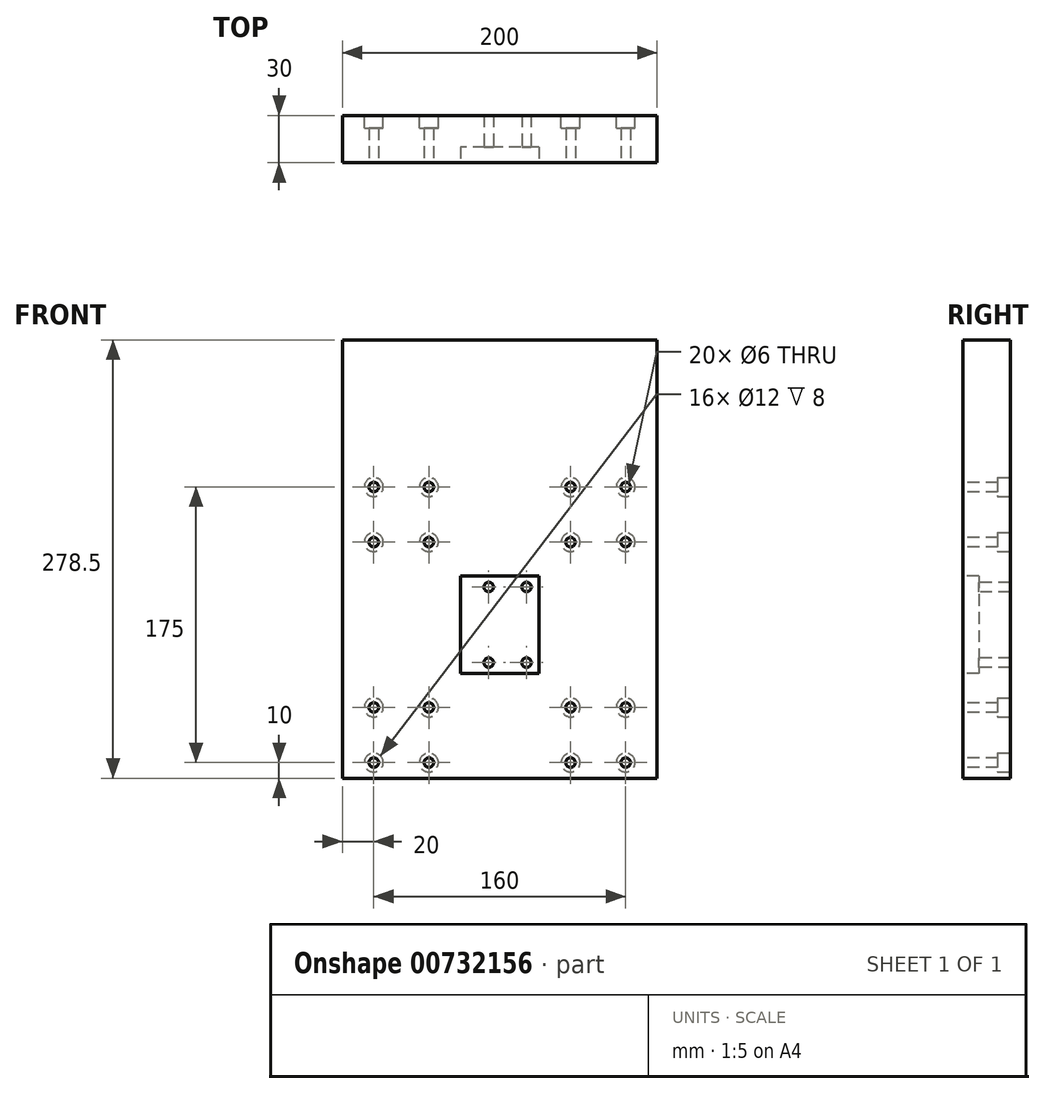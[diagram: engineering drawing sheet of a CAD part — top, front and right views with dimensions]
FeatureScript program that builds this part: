
annotation { "Feature Type Name" : "Feature", "Feature Type Description" : "" }
export const myFeature = defineFeature(function(context is Context, id is Id, definition is map)
    precondition{}
    {
        {
            var Q0;
            Q0=qCreatedBy(makeId("Front.planeOp"),FACE);
            var sketch = newSketch(context, id + "F0", { "sketchPlane" : qUnion([Q0])});
            skLineSegment(sketch, "E0.bottom", {"start": v(0, 0) * mm, "end": v(200, 0) * mm});
            skLineSegment(sketch, "E0.top", {"start": v(0, 400) * mm, "end": v(200, 400) * mm});
            skLineSegment(sketch, "E0.left", {"start": v(0, 0) * mm, "end": v(0, 400) * mm});
            skLineSegment(sketch, "E0.right", {"start": v(200, 0) * mm, "end": v(200, 400) * mm});
            skSolve(sketch);
        }
        {
            var Q0;
            Q0=makeQuery(id+"F0.imprint","IMPRINT",FACE,{"disambiguationData":[TD([[makeQuery(id+"F0.imprint","IMPRINT",EDGE,{"derivedFrom":sQuery(id+"F0.wireOp",EDGE,"E0.bottom")}),1.0]])]});
            extrude(context, id + "F1", {"entities" : qUnion([Q0]), "depth" : 30 * mm, "offsetDistance" : 25 * mm});
        }
        {
            var Q0;
            Q0=makeQuery(id+"F1.opExtrude","CAP_FACE",FACE,{"disambiguationData":[OSD([sQuery(id+"F0.wireOp",EDGE,"E0.bottom"),sQuery(id+"F0.wireOp",EDGE,"E0.top"),sQuery(id+"F0.wireOp",EDGE,"E0.left"),sQuery(id+"F0.wireOp",EDGE,"E0.right")])],"isStart":false});
            var sketch = newSketch(context, id + "F2", { "sketchPlane" : qUnion([Q0])});
            skLineSegment(sketch, "E1.bottom", {"start": v(20, 10) * mm, "end": v(55, 10) * mm});
            skLineSegment(sketch, "E1.top", {"start": v(20, 45) * mm, "end": v(55, 45) * mm});
            skLineSegment(sketch, "E1.left", {"start": v(20, 10) * mm, "end": v(20, 45) * mm});
            skLineSegment(sketch, "E1.right", {"start": v(55, 10) * mm, "end": v(55, 45) * mm});
            skLineSegment(sketch, "E2.bottom", {"start": v(0, 0) * mm, "end": v(20, 0) * mm});
            skLineSegment(sketch, "E2.top", {"start": v(0, 10) * mm, "end": v(20, 10) * mm});
            skLineSegment(sketch, "E2.left", {"start": v(0, 0) * mm, "end": v(0, 10) * mm});
            skLineSegment(sketch, "E2.right", {"start": v(20, 0) * mm, "end": v(20, 10) * mm});
            skLineSegment(sketch, "E3.bottom", {"start": v(200, 0) * mm, "end": v(180, 0) * mm});
            skLineSegment(sketch, "E3.top", {"start": v(200, 10) * mm, "end": v(180, 10) * mm});
            skLineSegment(sketch, "E3.left", {"start": v(200, 0) * mm, "end": v(200, 10) * mm});
            skLineSegment(sketch, "E3.right", {"start": v(180, 0) * mm, "end": v(180, 10) * mm});
            skLineSegment(sketch, "E4.bottom", {"start": v(180, 10) * mm, "end": v(145, 10) * mm});
            skLineSegment(sketch, "E4.top", {"start": v(180, 45) * mm, "end": v(145, 45) * mm});
            skLineSegment(sketch, "E4.left", {"start": v(180, 10) * mm, "end": v(180, 45) * mm});
            skLineSegment(sketch, "E4.right", {"start": v(145, 10) * mm, "end": v(145, 45) * mm});
            skCircle(sketch, "E5", {"center": v(20, 45) * mm, "radius": 3 * mm});
            skCircle(sketch, "E6", {"center": v(55, 45) * mm, "radius": 3 * mm});
            skCircle(sketch, "E7", {"center": v(20, 10) * mm, "radius": 3 * mm});
            skCircle(sketch, "E8", {"center": v(55, 10) * mm, "radius": 3 * mm});
            skCircle(sketch, "E9", {"center": v(145, 45) * mm, "radius": 3 * mm});
            skCircle(sketch, "E10", {"center": v(180, 45) * mm, "radius": 3 * mm});
            skCircle(sketch, "E11", {"center": v(145, 10) * mm, "radius": 3 * mm});
            skCircle(sketch, "E12", {"center": v(180, 10) * mm, "radius": 3 * mm});
            skLineSegment(sketch, "E13.bottom", {"start": v(55, 45) * mm, "end": v(20, 45) * mm});
            skLineSegment(sketch, "E13.top", {"start": v(55, 150) * mm, "end": v(20, 150) * mm});
            skLineSegment(sketch, "E13.left", {"start": v(55, 45) * mm, "end": v(55, 150) * mm});
            skLineSegment(sketch, "E13.right", {"start": v(20, 45) * mm, "end": v(20, 150) * mm});
            skLineSegment(sketch, "E14.bottom", {"start": v(145, 45) * mm, "end": v(180, 45) * mm});
            skLineSegment(sketch, "E14.top", {"start": v(145, 150) * mm, "end": v(180, 150) * mm});
            skLineSegment(sketch, "E14.left", {"start": v(145, 45) * mm, "end": v(145, 150) * mm});
            skLineSegment(sketch, "E14.right", {"start": v(180, 45) * mm, "end": v(180, 150) * mm});
            skLineSegment(sketch, "E15.bottom", {"start": v(20, 150) * mm, "end": v(55, 150) * mm});
            skLineSegment(sketch, "E15.top", {"start": v(20, 185) * mm, "end": v(55, 185) * mm});
            skLineSegment(sketch, "E15.left", {"start": v(20, 150) * mm, "end": v(20, 185) * mm});
            skLineSegment(sketch, "E15.right", {"start": v(55, 150) * mm, "end": v(55, 185) * mm});
            skLineSegment(sketch, "E16.top", {"start": v(145, 185) * mm, "end": v(180, 185) * mm});
            skLineSegment(sketch, "E16.left", {"start": v(145, 150) * mm, "end": v(145, 185) * mm});
            skLineSegment(sketch, "E16.right", {"start": v(180, 150) * mm, "end": v(180, 185) * mm});
            skCircle(sketch, "E17", {"center": v(20, 185) * mm, "radius": 3 * mm});
            skCircle(sketch, "E18", {"center": v(55, 185) * mm, "radius": 3 * mm});
            skCircle(sketch, "E19", {"center": v(20, 150) * mm, "radius": 3 * mm});
            skCircle(sketch, "E20", {"center": v(55, 150) * mm, "radius": 3 * mm});
            skCircle(sketch, "E21", {"center": v(145, 185) * mm, "radius": 3 * mm});
            skCircle(sketch, "E22", {"center": v(180, 185) * mm, "radius": 3 * mm});
            skCircle(sketch, "E23", {"center": v(145, 150) * mm, "radius": 3 * mm});
            skCircle(sketch, "E24", {"center": v(180, 150) * mm, "radius": 3 * mm});
            skSolve(sketch);
        }
        {
            var Q0;
            {var subQ0=sQuery(id+"F2.wireOp",EDGE,"E15.left");var subQ1=sQuery(id+"F2.wireOp",EDGE,"E15.top");var subQ2=makeQuery(id+"F2.imprint","INTERSECT",VERTEX,{"derivedFrom":[subQ1,subQ0]});Q0=makeQuery(id+"F2.imprint","IMPRINT",FACE,{"disambiguationData":[TD([[makeQuery(id+"F2.imprint","IMPRINT",EDGE,{"disambiguationData":[TD([[subQ2,-1.0]])],"derivedFrom":subQ1}),1.0]])]});}
            var Q1;
            {var subQ0=sQuery(id+"F2.wireOp",EDGE,"E15.left");var subQ1=sQuery(id+"F2.wireOp",EDGE,"E15.top");var subQ2=makeQuery(id+"F2.imprint","INTERSECT",VERTEX,{"derivedFrom":[subQ1,subQ0]});Q1=makeQuery(id+"F2.imprint","IMPRINT",FACE,{"disambiguationData":[TD([[makeQuery(id+"F2.imprint","IMPRINT",EDGE,{"disambiguationData":[TD([[subQ2,-1.0]])],"derivedFrom":subQ1}),-1.0]])]});}
            var Q2;
            {var subQ1=sQuery(id+"F2.wireOp",EDGE,"E13.right");var subQ3=sQuery(id+"F2.wireOp",EDGE,"E19");var subQ4=makeQuery(id+"F2.imprint","INTERSECT",VERTEX,{"derivedFrom":[subQ1,subQ3]});Q2=makeQuery(id+"F2.imprint","IMPRINT",FACE,{"disambiguationData":[TD([[makeQuery(id+"F2.imprint","IMPRINT",EDGE,{"disambiguationData":[TD([[subQ4,1.0]])],"derivedFrom":subQ3}),1.0]])]});}
            var Q3;
            {var subQ1=sQuery(id+"F2.wireOp",EDGE,"E15.bottom");var subQ3=sQuery(id+"F2.wireOp",EDGE,"E19");var subQ4=makeQuery(id+"F2.imprint","INTERSECT",VERTEX,{"derivedFrom":[subQ1,subQ3]});Q3=makeQuery(id+"F2.imprint","IMPRINT",FACE,{"disambiguationData":[TD([[makeQuery(id+"F2.imprint","IMPRINT",EDGE,{"disambiguationData":[TD([[subQ4,-1.0]])],"derivedFrom":subQ3}),1.0]])]});}
            var Q4;
            {var subQ1=sQuery(id+"F2.wireOp",EDGE,"E13.right");var subQ3=sQuery(id+"F2.wireOp",EDGE,"E19");var subQ4=makeQuery(id+"F2.imprint","INTERSECT",VERTEX,{"derivedFrom":[subQ1,subQ3]});Q4=makeQuery(id+"F2.imprint","IMPRINT",FACE,{"disambiguationData":[TD([[makeQuery(id+"F2.imprint","IMPRINT",EDGE,{"disambiguationData":[TD([[subQ4,-1.0]])],"derivedFrom":subQ3}),1.0]])]});}
            var Q5;
            {var subQ1=sQuery(id+"F2.wireOp",EDGE,"E13.left");var subQ3=sQuery(id+"F2.wireOp",EDGE,"E20");var subQ4=makeQuery(id+"F2.imprint","INTERSECT",VERTEX,{"derivedFrom":[subQ1,subQ3]});Q5=makeQuery(id+"F2.imprint","IMPRINT",FACE,{"disambiguationData":[TD([[makeQuery(id+"F2.imprint","IMPRINT",EDGE,{"disambiguationData":[TD([[subQ4,1.0]])],"derivedFrom":subQ3}),1.0]])]});}
            var Q6;
            {var subQ1=sQuery(id+"F2.wireOp",EDGE,"E15.bottom");var subQ3=sQuery(id+"F2.wireOp",EDGE,"E20");var subQ4=makeQuery(id+"F2.imprint","INTERSECT",VERTEX,{"derivedFrom":[subQ1,subQ3]});Q6=makeQuery(id+"F2.imprint","IMPRINT",FACE,{"disambiguationData":[TD([[makeQuery(id+"F2.imprint","IMPRINT",EDGE,{"disambiguationData":[TD([[subQ4,1.0]])],"derivedFrom":subQ3}),1.0]])]});}
            var Q7;
            {var subQ1=sQuery(id+"F2.wireOp",EDGE,"E13.left");var subQ3=sQuery(id+"F2.wireOp",EDGE,"E20");var subQ4=makeQuery(id+"F2.imprint","INTERSECT",VERTEX,{"derivedFrom":[subQ1,subQ3]});Q7=makeQuery(id+"F2.imprint","IMPRINT",FACE,{"disambiguationData":[TD([[makeQuery(id+"F2.imprint","IMPRINT",EDGE,{"disambiguationData":[TD([[subQ4,-1.0]])],"derivedFrom":subQ3}),1.0]])]});}
            var Q8;
            {var subQ0=sQuery(id+"F2.wireOp",EDGE,"E15.right");var subQ1=sQuery(id+"F2.wireOp",EDGE,"E15.top");var subQ2=makeQuery(id+"F2.imprint","INTERSECT",VERTEX,{"derivedFrom":[subQ1,subQ0]});Q8=makeQuery(id+"F2.imprint","IMPRINT",FACE,{"disambiguationData":[TD([[makeQuery(id+"F2.imprint","IMPRINT",EDGE,{"disambiguationData":[TD([[subQ2,1.0]])],"derivedFrom":subQ1}),-1.0]])]});}
            var Q9;
            {var subQ0=sQuery(id+"F2.wireOp",EDGE,"E15.right");var subQ1=sQuery(id+"F2.wireOp",EDGE,"E15.top");var subQ2=makeQuery(id+"F2.imprint","INTERSECT",VERTEX,{"derivedFrom":[subQ1,subQ0]});Q9=makeQuery(id+"F2.imprint","IMPRINT",FACE,{"disambiguationData":[TD([[makeQuery(id+"F2.imprint","IMPRINT",EDGE,{"disambiguationData":[TD([[subQ2,1.0]])],"derivedFrom":subQ1}),1.0]])]});}
            var Q10;
            {var subQ0=sQuery(id+"F2.wireOp",EDGE,"E16.left");var subQ1=sQuery(id+"F2.wireOp",EDGE,"E16.top");var subQ2=makeQuery(id+"F2.imprint","INTERSECT",VERTEX,{"derivedFrom":[subQ1,subQ0]});Q10=makeQuery(id+"F2.imprint","IMPRINT",FACE,{"disambiguationData":[TD([[makeQuery(id+"F2.imprint","IMPRINT",EDGE,{"disambiguationData":[TD([[subQ2,-1.0]])],"derivedFrom":subQ1}),1.0]])]});}
            var Q11;
            {var subQ0=sQuery(id+"F2.wireOp",EDGE,"E16.left");var subQ1=sQuery(id+"F2.wireOp",EDGE,"E16.top");var subQ2=makeQuery(id+"F2.imprint","INTERSECT",VERTEX,{"derivedFrom":[subQ1,subQ0]});Q11=makeQuery(id+"F2.imprint","IMPRINT",FACE,{"disambiguationData":[TD([[makeQuery(id+"F2.imprint","IMPRINT",EDGE,{"disambiguationData":[TD([[subQ2,-1.0]])],"derivedFrom":subQ1}),-1.0]])]});}
            var Q12;
            {var subQ0=sQuery(id+"F2.wireOp",EDGE,"E16.right");var subQ1=sQuery(id+"F2.wireOp",EDGE,"E16.top");var subQ2=makeQuery(id+"F2.imprint","INTERSECT",VERTEX,{"derivedFrom":[subQ1,subQ0]});Q12=makeQuery(id+"F2.imprint","IMPRINT",FACE,{"disambiguationData":[TD([[makeQuery(id+"F2.imprint","IMPRINT",EDGE,{"disambiguationData":[TD([[subQ2,1.0]])],"derivedFrom":subQ1}),-1.0]])]});}
            var Q13;
            {var subQ0=sQuery(id+"F2.wireOp",EDGE,"E16.right");var subQ1=sQuery(id+"F2.wireOp",EDGE,"E16.top");var subQ2=makeQuery(id+"F2.imprint","INTERSECT",VERTEX,{"derivedFrom":[subQ1,subQ0]});Q13=makeQuery(id+"F2.imprint","IMPRINT",FACE,{"disambiguationData":[TD([[makeQuery(id+"F2.imprint","IMPRINT",EDGE,{"disambiguationData":[TD([[subQ2,1.0]])],"derivedFrom":subQ1}),1.0]])]});}
            var Q14;
            {var subQ1=sQuery(id+"F2.wireOp",EDGE,"E14.right");var subQ3=sQuery(id+"F2.wireOp",EDGE,"E24");var subQ4=makeQuery(id+"F2.imprint","INTERSECT",VERTEX,{"derivedFrom":[subQ1,subQ3]});Q14=makeQuery(id+"F2.imprint","IMPRINT",FACE,{"disambiguationData":[TD([[makeQuery(id+"F2.imprint","IMPRINT",EDGE,{"disambiguationData":[TD([[subQ4,1.0]])],"derivedFrom":subQ3}),1.0]])]});}
            var Q15;
            {var subQ1=sQuery(id+"F2.wireOp",EDGE,"E14.top");var subQ3=sQuery(id+"F2.wireOp",EDGE,"E24");var subQ4=makeQuery(id+"F2.imprint","INTERSECT",VERTEX,{"derivedFrom":[subQ1,subQ3]});Q15=makeQuery(id+"F2.imprint","IMPRINT",FACE,{"disambiguationData":[TD([[makeQuery(id+"F2.imprint","IMPRINT",EDGE,{"disambiguationData":[TD([[subQ4,1.0]])],"derivedFrom":subQ3}),1.0]])]});}
            var Q16;
            {var subQ1=sQuery(id+"F2.wireOp",EDGE,"E14.right");var subQ3=sQuery(id+"F2.wireOp",EDGE,"E24");var subQ4=makeQuery(id+"F2.imprint","INTERSECT",VERTEX,{"derivedFrom":[subQ1,subQ3]});Q16=makeQuery(id+"F2.imprint","IMPRINT",FACE,{"disambiguationData":[TD([[makeQuery(id+"F2.imprint","IMPRINT",EDGE,{"disambiguationData":[TD([[subQ4,-1.0]])],"derivedFrom":subQ3}),1.0]])]});}
            var Q17;
            {var subQ1=sQuery(id+"F2.wireOp",EDGE,"E14.left");var subQ3=sQuery(id+"F2.wireOp",EDGE,"E23");var subQ4=makeQuery(id+"F2.imprint","INTERSECT",VERTEX,{"derivedFrom":[subQ1,subQ3]});Q17=makeQuery(id+"F2.imprint","IMPRINT",FACE,{"disambiguationData":[TD([[makeQuery(id+"F2.imprint","IMPRINT",EDGE,{"disambiguationData":[TD([[subQ4,-1.0]])],"derivedFrom":subQ3}),1.0]])]});}
            var Q18;
            {var subQ1=sQuery(id+"F2.wireOp",EDGE,"E14.top");var subQ3=sQuery(id+"F2.wireOp",EDGE,"E23");var subQ4=makeQuery(id+"F2.imprint","INTERSECT",VERTEX,{"derivedFrom":[subQ1,subQ3]});Q18=makeQuery(id+"F2.imprint","IMPRINT",FACE,{"disambiguationData":[TD([[makeQuery(id+"F2.imprint","IMPRINT",EDGE,{"disambiguationData":[TD([[subQ4,-1.0]])],"derivedFrom":subQ3}),1.0]])]});}
            var Q19;
            {var subQ1=sQuery(id+"F2.wireOp",EDGE,"E14.left");var subQ3=sQuery(id+"F2.wireOp",EDGE,"E23");var subQ4=makeQuery(id+"F2.imprint","INTERSECT",VERTEX,{"derivedFrom":[subQ1,subQ3]});Q19=makeQuery(id+"F2.imprint","IMPRINT",FACE,{"disambiguationData":[TD([[makeQuery(id+"F2.imprint","IMPRINT",EDGE,{"disambiguationData":[TD([[subQ4,1.0]])],"derivedFrom":subQ3}),1.0]])]});}
            var Q20;
            {var subQ1=sQuery(id+"F2.wireOp",EDGE,"E4.left");var subQ3=sQuery(id+"F2.wireOp",EDGE,"E10");var subQ4=makeQuery(id+"F2.imprint","INTERSECT",VERTEX,{"derivedFrom":[subQ1,subQ3]});Q20=makeQuery(id+"F2.imprint","IMPRINT",FACE,{"disambiguationData":[TD([[makeQuery(id+"F2.imprint","IMPRINT",EDGE,{"disambiguationData":[TD([[subQ4,-1.0]])],"derivedFrom":subQ3}),1.0]])]});}
            var Q21;
            {var subQ1=sQuery(id+"F2.wireOp",EDGE,"E4.left");var subQ3=sQuery(id+"F2.wireOp",EDGE,"E10");var subQ4=makeQuery(id+"F2.imprint","INTERSECT",VERTEX,{"derivedFrom":[subQ1,subQ3]});Q21=makeQuery(id+"F2.imprint","IMPRINT",FACE,{"disambiguationData":[TD([[makeQuery(id+"F2.imprint","IMPRINT",EDGE,{"disambiguationData":[TD([[subQ4,1.0]])],"derivedFrom":subQ3}),1.0]])]});}
            var Q22;
            {var subQ0=sQuery(id+"F2.wireOp",EDGE,"E14.bottom");var subQ1=sQuery(id+"F2.wireOp",EDGE,"E10");var subQ2=makeQuery(id+"F2.imprint","INTERSECT",VERTEX,{"derivedFrom":[subQ1,subQ0]});Q22=makeQuery(id+"F2.imprint","IMPRINT",FACE,{"disambiguationData":[TD([[makeQuery(id+"F2.imprint","IMPRINT",EDGE,{"disambiguationData":[TD([[subQ2,1.0]])],"derivedFrom":subQ1}),1.0]])]});}
            var Q23;
            {var subQ1=sQuery(id+"F2.wireOp",EDGE,"E4.right");var subQ3=sQuery(id+"F2.wireOp",EDGE,"E9");var subQ4=makeQuery(id+"F2.imprint","INTERSECT",VERTEX,{"derivedFrom":[subQ1,subQ3]});Q23=makeQuery(id+"F2.imprint","IMPRINT",FACE,{"disambiguationData":[TD([[makeQuery(id+"F2.imprint","IMPRINT",EDGE,{"disambiguationData":[TD([[subQ4,-1.0]])],"derivedFrom":subQ3}),1.0]])]});}
            var Q24;
            {var subQ0=sQuery(id+"F2.wireOp",EDGE,"E14.left");var subQ1=sQuery(id+"F2.wireOp",EDGE,"E9");var subQ2=makeQuery(id+"F2.imprint","INTERSECT",VERTEX,{"derivedFrom":[subQ1,subQ0]});Q24=makeQuery(id+"F2.imprint","IMPRINT",FACE,{"disambiguationData":[TD([[makeQuery(id+"F2.imprint","IMPRINT",EDGE,{"disambiguationData":[TD([[subQ2,1.0]])],"derivedFrom":subQ1}),1.0]])]});}
            var Q25;
            {var subQ1=sQuery(id+"F2.wireOp",EDGE,"E4.right");var subQ3=sQuery(id+"F2.wireOp",EDGE,"E9");var subQ4=makeQuery(id+"F2.imprint","INTERSECT",VERTEX,{"derivedFrom":[subQ1,subQ3]});Q25=makeQuery(id+"F2.imprint","IMPRINT",FACE,{"disambiguationData":[TD([[makeQuery(id+"F2.imprint","IMPRINT",EDGE,{"disambiguationData":[TD([[subQ4,1.0]])],"derivedFrom":subQ3}),1.0]])]});}
            var Q26;
            {var subQ0=sQuery(id+"F2.wireOp",EDGE,"E4.right");var subQ1=sQuery(id+"F2.wireOp",EDGE,"E4.bottom");var subQ2=makeQuery(id+"F2.imprint","INTERSECT",VERTEX,{"derivedFrom":[subQ1,subQ0]});Q26=makeQuery(id+"F2.imprint","IMPRINT",FACE,{"disambiguationData":[TD([[makeQuery(id+"F2.imprint","IMPRINT",EDGE,{"disambiguationData":[TD([[subQ2,1.0]])],"derivedFrom":subQ1}),1.0]])]});}
            var Q27;
            {var subQ0=sQuery(id+"F2.wireOp",EDGE,"E4.right");var subQ1=sQuery(id+"F2.wireOp",EDGE,"E4.bottom");var subQ2=makeQuery(id+"F2.imprint","INTERSECT",VERTEX,{"derivedFrom":[subQ1,subQ0]});Q27=makeQuery(id+"F2.imprint","IMPRINT",FACE,{"disambiguationData":[TD([[makeQuery(id+"F2.imprint","IMPRINT",EDGE,{"disambiguationData":[TD([[subQ2,1.0]])],"derivedFrom":subQ1}),-1.0]])]});}
            var Q28;
            {var subQ1=sQuery(id+"F2.wireOp",EDGE,"E3.right");var subQ3=sQuery(id+"F2.wireOp",EDGE,"E12");var subQ4=makeQuery(id+"F2.imprint","INTERSECT",VERTEX,{"derivedFrom":[subQ1,subQ3]});Q28=makeQuery(id+"F2.imprint","IMPRINT",FACE,{"disambiguationData":[TD([[makeQuery(id+"F2.imprint","IMPRINT",EDGE,{"disambiguationData":[TD([[subQ4,1.0]])],"derivedFrom":subQ3}),1.0]])]});}
            var Q29;
            {var subQ1=sQuery(id+"F2.wireOp",EDGE,"E3.top");var subQ3=sQuery(id+"F2.wireOp",EDGE,"E12");var subQ4=makeQuery(id+"F2.imprint","INTERSECT",VERTEX,{"derivedFrom":[subQ1,subQ3]});Q29=makeQuery(id+"F2.imprint","IMPRINT",FACE,{"disambiguationData":[TD([[makeQuery(id+"F2.imprint","IMPRINT",EDGE,{"disambiguationData":[TD([[subQ4,-1.0]])],"derivedFrom":subQ3}),1.0]])]});}
            var Q30;
            {var subQ1=sQuery(id+"F2.wireOp",EDGE,"E4.bottom");var subQ3=sQuery(id+"F2.wireOp",EDGE,"E12");var subQ4=makeQuery(id+"F2.imprint","INTERSECT",VERTEX,{"derivedFrom":[subQ1,subQ3]});Q30=makeQuery(id+"F2.imprint","IMPRINT",FACE,{"disambiguationData":[TD([[makeQuery(id+"F2.imprint","IMPRINT",EDGE,{"disambiguationData":[TD([[subQ4,1.0]])],"derivedFrom":subQ3}),1.0]])]});}
            var Q31;
            {var subQ1=sQuery(id+"F2.wireOp",EDGE,"E3.top");var subQ3=sQuery(id+"F2.wireOp",EDGE,"E12");var subQ4=makeQuery(id+"F2.imprint","INTERSECT",VERTEX,{"derivedFrom":[subQ1,subQ3]});Q31=makeQuery(id+"F2.imprint","IMPRINT",FACE,{"disambiguationData":[TD([[makeQuery(id+"F2.imprint","IMPRINT",EDGE,{"disambiguationData":[TD([[subQ4,1.0]])],"derivedFrom":subQ3}),1.0]])]});}
            var Q32;
            {var subQ1=sQuery(id+"F2.wireOp",EDGE,"E1.left");var subQ3=sQuery(id+"F2.wireOp",EDGE,"E7");var subQ4=makeQuery(id+"F2.imprint","INTERSECT",VERTEX,{"derivedFrom":[subQ1,subQ3]});Q32=makeQuery(id+"F2.imprint","IMPRINT",FACE,{"disambiguationData":[TD([[makeQuery(id+"F2.imprint","IMPRINT",EDGE,{"disambiguationData":[TD([[subQ4,-1.0]])],"derivedFrom":subQ3}),1.0]])]});}
            var Q33;
            {var subQ1=sQuery(id+"F2.wireOp",EDGE,"E2.top");var subQ3=sQuery(id+"F2.wireOp",EDGE,"E7");var subQ4=makeQuery(id+"F2.imprint","INTERSECT",VERTEX,{"derivedFrom":[subQ1,subQ3]});Q33=makeQuery(id+"F2.imprint","IMPRINT",FACE,{"disambiguationData":[TD([[makeQuery(id+"F2.imprint","IMPRINT",EDGE,{"disambiguationData":[TD([[subQ4,-1.0]])],"derivedFrom":subQ3}),1.0]])]});}
            var Q34;
            {var subQ1=sQuery(id+"F2.wireOp",EDGE,"E1.bottom");var subQ3=sQuery(id+"F2.wireOp",EDGE,"E7");var subQ4=makeQuery(id+"F2.imprint","INTERSECT",VERTEX,{"derivedFrom":[subQ1,subQ3]});Q34=makeQuery(id+"F2.imprint","IMPRINT",FACE,{"disambiguationData":[TD([[makeQuery(id+"F2.imprint","IMPRINT",EDGE,{"disambiguationData":[TD([[subQ4,1.0]])],"derivedFrom":subQ3}),1.0]])]});}
            var Q35;
            {var subQ1=sQuery(id+"F2.wireOp",EDGE,"E1.bottom");var subQ3=sQuery(id+"F2.wireOp",EDGE,"E7");var subQ4=makeQuery(id+"F2.imprint","INTERSECT",VERTEX,{"derivedFrom":[subQ1,subQ3]});Q35=makeQuery(id+"F2.imprint","IMPRINT",FACE,{"disambiguationData":[TD([[makeQuery(id+"F2.imprint","IMPRINT",EDGE,{"disambiguationData":[TD([[subQ4,-1.0]])],"derivedFrom":subQ3}),1.0]])]});}
            var Q36;
            {var subQ0=sQuery(id+"F2.wireOp",EDGE,"E1.right");var subQ1=sQuery(id+"F2.wireOp",EDGE,"E1.bottom");var subQ2=makeQuery(id+"F2.imprint","INTERSECT",VERTEX,{"derivedFrom":[subQ1,subQ0]});Q36=makeQuery(id+"F2.imprint","IMPRINT",FACE,{"disambiguationData":[TD([[makeQuery(id+"F2.imprint","IMPRINT",EDGE,{"disambiguationData":[TD([[subQ2,1.0]])],"derivedFrom":subQ1}),-1.0]])]});}
            var Q37;
            {var subQ0=sQuery(id+"F2.wireOp",EDGE,"E1.right");var subQ1=sQuery(id+"F2.wireOp",EDGE,"E1.bottom");var subQ2=makeQuery(id+"F2.imprint","INTERSECT",VERTEX,{"derivedFrom":[subQ1,subQ0]});Q37=makeQuery(id+"F2.imprint","IMPRINT",FACE,{"disambiguationData":[TD([[makeQuery(id+"F2.imprint","IMPRINT",EDGE,{"disambiguationData":[TD([[subQ2,1.0]])],"derivedFrom":subQ1}),1.0]])]});}
            var Q38;
            {var subQ1=sQuery(id+"F2.wireOp",EDGE,"E1.right");var subQ3=sQuery(id+"F2.wireOp",EDGE,"E6");var subQ4=makeQuery(id+"F2.imprint","INTERSECT",VERTEX,{"derivedFrom":[subQ1,subQ3]});Q38=makeQuery(id+"F2.imprint","IMPRINT",FACE,{"disambiguationData":[TD([[makeQuery(id+"F2.imprint","IMPRINT",EDGE,{"disambiguationData":[TD([[subQ4,-1.0]])],"derivedFrom":subQ3}),1.0]])]});}
            var Q39;
            {var subQ1=sQuery(id+"F2.wireOp",EDGE,"E1.right");var subQ3=sQuery(id+"F2.wireOp",EDGE,"E6");var subQ4=makeQuery(id+"F2.imprint","INTERSECT",VERTEX,{"derivedFrom":[subQ1,subQ3]});Q39=makeQuery(id+"F2.imprint","IMPRINT",FACE,{"disambiguationData":[TD([[makeQuery(id+"F2.imprint","IMPRINT",EDGE,{"disambiguationData":[TD([[subQ4,1.0]])],"derivedFrom":subQ3}),1.0]])]});}
            var Q40;
            {var subQ0=sQuery(id+"F2.wireOp",EDGE,"E13.bottom");var subQ1=sQuery(id+"F2.wireOp",EDGE,"E6");var subQ2=makeQuery(id+"F2.imprint","INTERSECT",VERTEX,{"derivedFrom":[subQ1,subQ0]});Q40=makeQuery(id+"F2.imprint","IMPRINT",FACE,{"disambiguationData":[TD([[makeQuery(id+"F2.imprint","IMPRINT",EDGE,{"disambiguationData":[TD([[subQ2,1.0]])],"derivedFrom":subQ1}),1.0]])]});}
            var Q41;
            {var subQ1=sQuery(id+"F2.wireOp",EDGE,"E1.left");var subQ3=sQuery(id+"F2.wireOp",EDGE,"E5");var subQ4=makeQuery(id+"F2.imprint","INTERSECT",VERTEX,{"derivedFrom":[subQ1,subQ3]});Q41=makeQuery(id+"F2.imprint","IMPRINT",FACE,{"disambiguationData":[TD([[makeQuery(id+"F2.imprint","IMPRINT",EDGE,{"disambiguationData":[TD([[subQ4,-1.0]])],"derivedFrom":subQ3}),1.0]])]});}
            var Q42;
            {var subQ1=sQuery(id+"F2.wireOp",EDGE,"E1.left");var subQ3=sQuery(id+"F2.wireOp",EDGE,"E5");var subQ4=makeQuery(id+"F2.imprint","INTERSECT",VERTEX,{"derivedFrom":[subQ1,subQ3]});Q42=makeQuery(id+"F2.imprint","IMPRINT",FACE,{"disambiguationData":[TD([[makeQuery(id+"F2.imprint","IMPRINT",EDGE,{"disambiguationData":[TD([[subQ4,1.0]])],"derivedFrom":subQ3}),1.0]])]});}
            var Q43;
            {var subQ0=sQuery(id+"F2.wireOp",EDGE,"E13.right");var subQ1=sQuery(id+"F2.wireOp",EDGE,"E5");var subQ2=makeQuery(id+"F2.imprint","INTERSECT",VERTEX,{"derivedFrom":[subQ1,subQ0]});Q43=makeQuery(id+"F2.imprint","IMPRINT",FACE,{"disambiguationData":[TD([[makeQuery(id+"F2.imprint","IMPRINT",EDGE,{"disambiguationData":[TD([[subQ2,1.0]])],"derivedFrom":subQ1}),1.0]])]});}
            extrude(context, id + "F3", {"entities" : qUnion([Q0, Q1, Q2, Q3, Q4, Q5, Q6, Q7, Q8, Q9, Q10, Q11, Q12, Q13, Q14, Q15, Q16, Q17, Q18, Q19, Q20, Q21, Q22, Q23, Q24, Q25, Q26, Q27, Q28, Q29, Q30, Q31, Q32, Q33, Q34, Q35, Q36, Q37, Q38, Q39, Q40, Q41, Q42, Q43]), "operationType" : NewBodyOperationType.REMOVE, "oppositeDirection" : true, "depth" : 30 * mm, "offsetDistance" : 25 * mm});
        }
        {
            var Q0;
            Q0=makeQuery(id+"F1.opExtrude","CAP_FACE",FACE,{"disambiguationData":[OSD([sQuery(id+"F0.wireOp",EDGE,"E0.bottom"),sQuery(id+"F0.wireOp",EDGE,"E0.top"),sQuery(id+"F0.wireOp",EDGE,"E0.left"),sQuery(id+"F0.wireOp",EDGE,"E0.right")])],"isStart":false});
            var sketch = newSketch(context, id + "F4", { "sketchPlane" : qUnion([Q0])});
            skLineSegment(sketch, "E25", {"start": v(55, 150) * mm, "end": v(145, 150) * mm});
            skLineSegment(sketch, "E26", {"start": v(55, 150) * mm, "end": v(55, 45) * mm});
            skLineSegment(sketch, "E27.bottom", {"start": v(125, 128.5) * mm, "end": v(75, 128.5) * mm});
            skLineSegment(sketch, "E27.top", {"start": v(125, 66.5) * mm, "end": v(75, 66.5) * mm});
            skLineSegment(sketch, "E27.left", {"start": v(125, 128.5) * mm, "end": v(125, 66.5) * mm});
            skLineSegment(sketch, "E27.right", {"start": v(75, 128.5) * mm, "end": v(75, 66.5) * mm});
            skPoint(sketch, "E27.middle", {"position": v(100, 97.5) * mm});
            skPoint(sketch, "E27.middle.positionSnap0", {"position": v(100, 150) * mm});
            skPoint(sketch, "E27.middle.positionSnap1", {"position": v(55, 97.5) * mm});
            skPoint(sketch, "E27.centerSnap0", {"position": v(100, 150) * mm});
            skPoint(sketch, "E27.centerSnap1", {"position": v(55, 97.5) * mm});
            skSolve(sketch);
        }
        {
            var Q0;
            Q0=makeQuery(id+"F4.imprint","IMPRINT",FACE,{"disambiguationData":[TD([[makeQuery(id+"F4.imprint","IMPRINT",EDGE,{"derivedFrom":sQuery(id+"F4.wireOp",EDGE,"E27.bottom")}),1.0]])]});
            extrude(context, id + "F5", {"entities" : qUnion([Q0]), "operationType" : NewBodyOperationType.REMOVE, "oppositeDirection" : true, "depth" : 10 * mm, "offsetDistance" : 25 * mm});
        }
        {
            var Q0;
            Q0=makeQuery(id+"F1.opExtrude","CAP_FACE",FACE,{"disambiguationData":[OSD([sQuery(id+"F0.wireOp",EDGE,"E0.bottom"),sQuery(id+"F0.wireOp",EDGE,"E0.top"),sQuery(id+"F0.wireOp",EDGE,"E0.left"),sQuery(id+"F0.wireOp",EDGE,"E0.right")])],"isStart":true});
            var sketch = newSketch(context, id + "F6", { "sketchPlane" : qUnion([Q0])});
            skCircle(sketch, "E28", {"center": v(-180, 185) * mm, "radius": 6 * mm});
            skCircle(sketch, "E29.0.1.0", {"center": v(-180, 150) * mm, "radius": 6 * mm});
            skCircle(sketch, "E29.1.0.0", {"center": v(-145, 185) * mm, "radius": 6 * mm});
            skCircle(sketch, "E29.1.1.0", {"center": v(-145, 150) * mm, "radius": 6 * mm});
            skLineSegment(sketch, "E29.direction1", {"start": v(-180, 185) * mm, "end": v(-145, 185) * mm, "construction": true});
            skLineSegment(sketch, "E29.direction2", {"start": v(-180, 185) * mm, "end": v(-180, 150) * mm, "construction": true});
            skCircle(sketch, "E30.0.1.0", {"center": v(-180, 45) * mm, "radius": 6 * mm});
            skCircle(sketch, "E30.0.1.1", {"center": v(-180, 10) * mm, "radius": 6 * mm});
            skCircle(sketch, "E30.0.1.2", {"center": v(-145, 45) * mm, "radius": 6 * mm});
            skCircle(sketch, "E30.0.1.3", {"center": v(-145, 10) * mm, "radius": 6 * mm});
            skLineSegment(sketch, "E30.0.1.4", {"start": v(-180, 45) * mm, "end": v(-145, 45) * mm, "construction": true});
            skLineSegment(sketch, "E30.0.1.5", {"start": v(-180, 45) * mm, "end": v(-180, 10) * mm, "construction": true});
            skCircle(sketch, "E30.1.0.0", {"center": v(-55, 185) * mm, "radius": 6 * mm});
            skCircle(sketch, "E30.1.0.1", {"center": v(-55, 150) * mm, "radius": 6 * mm});
            skCircle(sketch, "E30.1.0.2", {"center": v(-20, 185) * mm, "radius": 6 * mm});
            skCircle(sketch, "E30.1.0.3", {"center": v(-20, 150) * mm, "radius": 6 * mm});
            skLineSegment(sketch, "E30.1.0.4", {"start": v(-55, 185) * mm, "end": v(-20, 185) * mm, "construction": true});
            skLineSegment(sketch, "E30.1.0.5", {"start": v(-55, 185) * mm, "end": v(-55, 150) * mm, "construction": true});
            skCircle(sketch, "E30.1.1.0", {"center": v(-55, 45) * mm, "radius": 6 * mm});
            skCircle(sketch, "E30.1.1.1", {"center": v(-55, 10) * mm, "radius": 6 * mm});
            skCircle(sketch, "E30.1.1.2", {"center": v(-20, 45) * mm, "radius": 6 * mm});
            skCircle(sketch, "E30.1.1.3", {"center": v(-20, 10) * mm, "radius": 6 * mm});
            skLineSegment(sketch, "E30.1.1.4", {"start": v(-55, 45) * mm, "end": v(-20, 45) * mm, "construction": true});
            skLineSegment(sketch, "E30.1.1.5", {"start": v(-55, 45) * mm, "end": v(-55, 10) * mm, "construction": true});
            skLineSegment(sketch, "E30.direction1", {"start": v(-180, 150) * mm, "end": v(-55, 150) * mm, "construction": true});
            skLineSegment(sketch, "E30.direction2", {"start": v(-180, 150) * mm, "end": v(-180, 10) * mm, "construction": true});
            skSolve(sketch);
        }
        {
            var Q0;
            Q0 = qSketchRegion(id + "F6", true);
            extrude(context, id + "F7", {"entities" : qUnion([Q0]), "operationType" : NewBodyOperationType.REMOVE, "oppositeDirection" : true, "depth" : 8 * mm, "offsetDistance" : 25 * mm});
        }
        {
            var Q0;
            Q0=makeQuery(id+"F5.boolean.opBoolean","COPY",FACE,{"derivedFrom":makeQuery(id+"F5.opExtrude","CAP_FACE",FACE,{"disambiguationData":[OSD([sQuery(id+"F4.wireOp",EDGE,"E27.bottom"),sQuery(id+"F4.wireOp",EDGE,"E27.top"),sQuery(id+"F4.wireOp",EDGE,"E27.left"),sQuery(id+"F4.wireOp",EDGE,"E27.right")])],"isStart":false})});
            var sketch = newSketch(context, id + "F8", { "sketchPlane" : qUnion([Q0])});
            skLineSegment(sketch, "E31.bottom", {"start": v(93, 73.5) * mm, "end": v(117, 73.5) * mm});
            skLineSegment(sketch, "E31.top", {"start": v(93, 121.5) * mm, "end": v(117, 121.5) * mm});
            skLineSegment(sketch, "E31.left", {"start": v(93, 73.5) * mm, "end": v(93, 121.5) * mm});
            skLineSegment(sketch, "E31.right", {"start": v(117, 73.5) * mm, "end": v(117, 121.5) * mm});
            skCircle(sketch, "E32", {"center": v(93, 121.5) * mm, "radius": 3 * mm});
            skCircle(sketch, "E33", {"center": v(117, 121.5) * mm, "radius": 3 * mm});
            skCircle(sketch, "E34", {"center": v(93, 73.5) * mm, "radius": 3 * mm});
            skCircle(sketch, "E35", {"center": v(117, 73.5) * mm, "radius": 3 * mm});
            skSolve(sketch);
        }
        {
            var Q0;
            {var subQ0=sQuery(id+"F8.wireOp",EDGE,"E31.left");var subQ1=sQuery(id+"F8.wireOp",EDGE,"E31.top");var subQ2=makeQuery(id+"F8.imprint","INTERSECT",VERTEX,{"derivedFrom":[subQ1,subQ0]});Q0=makeQuery(id+"F8.imprint","IMPRINT",FACE,{"disambiguationData":[TD([[makeQuery(id+"F8.imprint","IMPRINT",EDGE,{"disambiguationData":[TD([[subQ2,-1.0]])],"derivedFrom":subQ1}),-1.0]])]});}
            var Q1;
            {var subQ0=sQuery(id+"F8.wireOp",EDGE,"E31.left");var subQ1=sQuery(id+"F8.wireOp",EDGE,"E31.top");var subQ2=makeQuery(id+"F8.imprint","INTERSECT",VERTEX,{"derivedFrom":[subQ1,subQ0]});Q1=makeQuery(id+"F8.imprint","IMPRINT",FACE,{"disambiguationData":[TD([[makeQuery(id+"F8.imprint","IMPRINT",EDGE,{"disambiguationData":[TD([[subQ2,-1.0]])],"derivedFrom":subQ1}),1.0]])]});}
            var Q2;
            {var subQ0=sQuery(id+"F8.wireOp",EDGE,"E31.right");var subQ1=sQuery(id+"F8.wireOp",EDGE,"E31.top");var subQ2=makeQuery(id+"F8.imprint","INTERSECT",VERTEX,{"derivedFrom":[subQ1,subQ0]});Q2=makeQuery(id+"F8.imprint","IMPRINT",FACE,{"disambiguationData":[TD([[makeQuery(id+"F8.imprint","IMPRINT",EDGE,{"disambiguationData":[TD([[subQ2,1.0]])],"derivedFrom":subQ1}),-1.0]])]});}
            var Q3;
            {var subQ0=sQuery(id+"F8.wireOp",EDGE,"E31.right");var subQ1=sQuery(id+"F8.wireOp",EDGE,"E31.top");var subQ2=makeQuery(id+"F8.imprint","INTERSECT",VERTEX,{"derivedFrom":[subQ1,subQ0]});Q3=makeQuery(id+"F8.imprint","IMPRINT",FACE,{"disambiguationData":[TD([[makeQuery(id+"F8.imprint","IMPRINT",EDGE,{"disambiguationData":[TD([[subQ2,1.0]])],"derivedFrom":subQ1}),1.0]])]});}
            var Q4;
            {var subQ0=sQuery(id+"F8.wireOp",EDGE,"E31.left");var subQ1=sQuery(id+"F8.wireOp",EDGE,"E31.bottom");var subQ2=makeQuery(id+"F8.imprint","INTERSECT",VERTEX,{"derivedFrom":[subQ1,subQ0]});Q4=makeQuery(id+"F8.imprint","IMPRINT",FACE,{"disambiguationData":[TD([[makeQuery(id+"F8.imprint","IMPRINT",EDGE,{"disambiguationData":[TD([[subQ2,-1.0]])],"derivedFrom":subQ1}),-1.0]])]});}
            var Q5;
            {var subQ0=sQuery(id+"F8.wireOp",EDGE,"E31.left");var subQ1=sQuery(id+"F8.wireOp",EDGE,"E31.bottom");var subQ2=makeQuery(id+"F8.imprint","INTERSECT",VERTEX,{"derivedFrom":[subQ1,subQ0]});Q5=makeQuery(id+"F8.imprint","IMPRINT",FACE,{"disambiguationData":[TD([[makeQuery(id+"F8.imprint","IMPRINT",EDGE,{"disambiguationData":[TD([[subQ2,-1.0]])],"derivedFrom":subQ1}),1.0]])]});}
            var Q6;
            {var subQ0=sQuery(id+"F8.wireOp",EDGE,"E31.right");var subQ1=sQuery(id+"F8.wireOp",EDGE,"E31.bottom");var subQ2=makeQuery(id+"F8.imprint","INTERSECT",VERTEX,{"derivedFrom":[subQ1,subQ0]});Q6=makeQuery(id+"F8.imprint","IMPRINT",FACE,{"disambiguationData":[TD([[makeQuery(id+"F8.imprint","IMPRINT",EDGE,{"disambiguationData":[TD([[subQ2,1.0]])],"derivedFrom":subQ1}),1.0]])]});}
            var Q7;
            {var subQ0=sQuery(id+"F8.wireOp",EDGE,"E31.right");var subQ1=sQuery(id+"F8.wireOp",EDGE,"E31.bottom");var subQ2=makeQuery(id+"F8.imprint","INTERSECT",VERTEX,{"derivedFrom":[subQ1,subQ0]});Q7=makeQuery(id+"F8.imprint","IMPRINT",FACE,{"disambiguationData":[TD([[makeQuery(id+"F8.imprint","IMPRINT",EDGE,{"disambiguationData":[TD([[subQ2,1.0]])],"derivedFrom":subQ1}),-1.0]])]});}
            extrude(context, id + "F9", {"entities" : qUnion([Q0, Q1, Q2, Q3, Q4, Q5, Q6, Q7]), "operationType" : NewBodyOperationType.REMOVE, "oppositeDirection" : true, "depth" : 30 * mm, "offsetDistance" : 25 * mm});
        }
        {
            var Q0;
            Q0=makeQuery(id+"F1.opExtrude","CAP_FACE",FACE,{"disambiguationData":[OSD([sQuery(id+"F0.wireOp",EDGE,"E0.bottom"),sQuery(id+"F0.wireOp",EDGE,"E0.top"),sQuery(id+"F0.wireOp",EDGE,"E0.left"),sQuery(id+"F0.wireOp",EDGE,"E0.right")])],"isStart":true});
            var sketch = newSketch(context, id + "F10", { "sketchPlane" : qUnion([Q0])});
            skLineSegment(sketch, "E36.bottom", {"start": v(-200, 400) * mm, "end": v(0, 400) * mm});
            skLineSegment(sketch, "E36.top", {"start": v(-200, 278.5) * mm, "end": v(0, 278.5) * mm});
            skLineSegment(sketch, "E36.left", {"start": v(-200, 400) * mm, "end": v(-200, 278.5) * mm});
            skLineSegment(sketch, "E36.right", {"start": v(0, 400) * mm, "end": v(0, 278.5) * mm});
            skSolve(sketch);
        }
        {
            var Q0;
            Q0=makeQuery(id+"F10.imprint","IMPRINT",FACE,{"disambiguationData":[TD([[makeQuery(id+"F10.imprint","IMPRINT",EDGE,{"derivedFrom":sQuery(id+"F10.wireOp",EDGE,"E36.bottom")}),1.0]])]});
            extrude(context, id + "F11", {"entities" : qUnion([Q0]), "operationType" : NewBodyOperationType.REMOVE, "oppositeDirection" : true, "depth" : 30 * mm, "offsetDistance" : 25 * mm});
        }
    });
